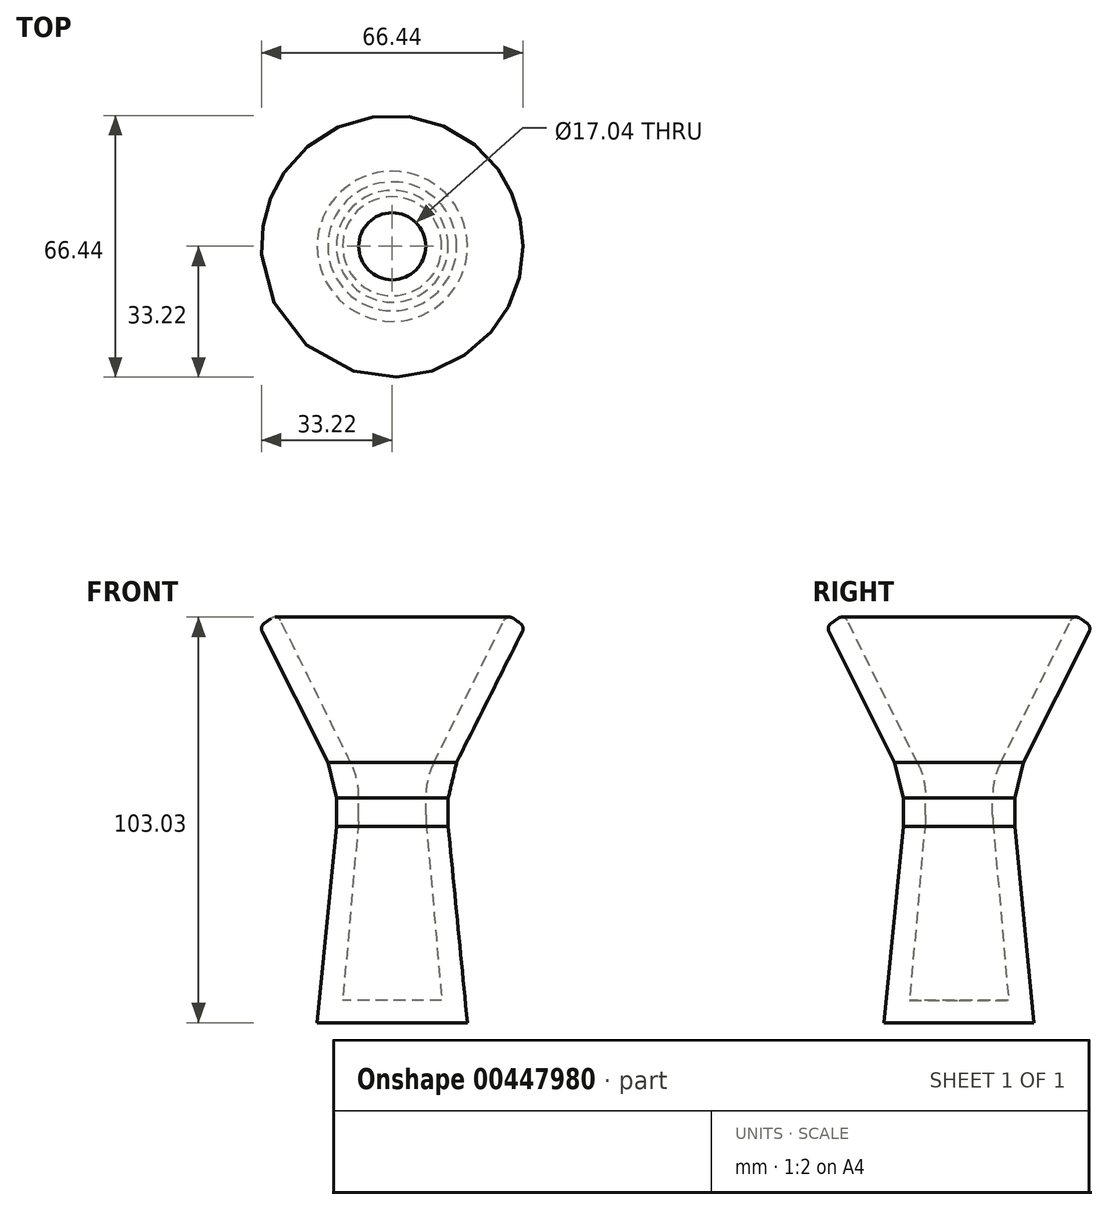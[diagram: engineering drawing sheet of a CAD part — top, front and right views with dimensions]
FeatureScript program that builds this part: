
annotation { "Feature Type Name" : "Feature", "Feature Type Description" : "" }
export const myFeature = defineFeature(function(context is Context, id is Id, definition is map)
    precondition{}
    {
        {
            var Q0;
            Q0=qCreatedBy(makeId("Front.planeOp"),FACE);
            var sketch = newSketch(context, id + "F0", { "sketchPlane" : qUnion([Q0])});
            skLineSegment(sketch, "E0", {"start": v(-29.2, 41.99) * mm, "end": v(-8.52, 0) * mm});
            skLineSegment(sketch, "E1", {"start": v(-8.52, 0) * mm, "end": v(-8.52, -9.94) * mm});
            skLineSegment(sketch, "E2", {"start": v(-8.52, -9.94) * mm, "end": v(-12.58, -56.19) * mm});
            skLineSegment(sketch, "E3", {"start": v(-12.58, -56.19) * mm, "end": v(0, -56.19) * mm});
            skLineSegment(sketch, "E4", {"start": v(0, -56.19) * mm, "end": v(0, -61.87) * mm});
            skLineSegment(sketch, "E5", {"start": v(0, -61.87) * mm, "end": v(-19.07, -61.87) * mm});
            skLineSegment(sketch, "E6", {"start": v(-19.07, -61.87) * mm, "end": v(-14.2, -11.97) * mm});
            skLineSegment(sketch, "E7", {"start": v(-14.2, -11.97) * mm, "end": v(-14.2, 0) * mm});
            skLineSegment(sketch, "E8", {"start": v(-14.2, 0) * mm, "end": v(-33.67, 38.74) * mm});
            skLineSegment(sketch, "E9", {"start": v(-33.67, 38.74) * mm, "end": v(-29.2, 41.99) * mm});
            skSolve(sketch);
        }
        {
            var Q0;
            Q0=makeQuery(id+"F0.imprint","IMPRINT",FACE,{"disambiguationData":[TD([[makeQuery(id+"F0.imprint","IMPRINT",EDGE,{"derivedFrom":sQuery(id+"F0.wireOp",EDGE,"E0")}),-1.0]])]});
            var Q1;
            Q1=sQuery(id+"F0.wireOp",EDGE,"E4");
            revolve(context, id + "F1", {"entities" : qUnion([Q0]), "axis" : qUnion([Q1]), "revolveType" : RevolveType.FULL});
        }
        {
            var Q0;
            Q0=makeQuery(id+"F1.opRevolve","SWEPT_EDGE",EDGE,{"disambiguationData":[OSD([sQuery(id+"F0.wireOp",EDGE,"E0"),sQuery(id+"F0.wireOp",EDGE,"E9")])]});
            var Q1;
            Q1=makeQuery(id+"F1.opRevolve","SWEPT_EDGE",EDGE,{"disambiguationData":[OSD([sQuery(id+"F0.wireOp",EDGE,"E8"),sQuery(id+"F0.wireOp",EDGE,"E9")])]});
            fillet(context, id + "F2", {"entities" : qUnion([Q0, Q1]), "radius" : 1.63 * mm, "tangentPropagation" : true, "allowEdgeOverflow" : false});
        }
        {
            var Q0;
            Q0=makeQuery(id+"F1.opRevolve","SWEPT_EDGE",EDGE,{"disambiguationData":[OSD([sQuery(id+"F0.wireOp",EDGE,"E7"),sQuery(id+"F0.wireOp",EDGE,"E8")])]});
            chamfer(context, id + "F3", {"entities" : qUnion([Q0]), "width" : 20.32 * mm, "tangentPropagation" : true});
        }
        {
            var Q0;
            Q0=makeQuery(id+"F1.opRevolve","SWEPT_EDGE",EDGE,{"disambiguationData":[OSD([sQuery(id+"F0.wireOp",EDGE,"E1"),sQuery(id+"F0.wireOp",EDGE,"E2")])]});
            var Q1;
            Q1=makeQuery(id+"F1.opRevolve","SWEPT_EDGE",EDGE,{"disambiguationData":[OSD([sQuery(id+"F0.wireOp",EDGE,"E0"),sQuery(id+"F0.wireOp",EDGE,"E1")])]});
            fillet(context, id + "F4", {"entities" : qUnion([Q0, Q1]), "radius" : 18.97 * mm, "tangentPropagation" : true, "allowEdgeOverflow" : false});
        }
    });
